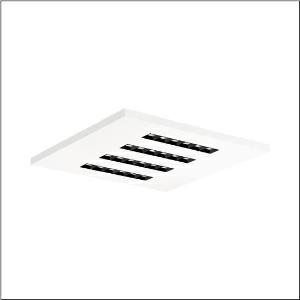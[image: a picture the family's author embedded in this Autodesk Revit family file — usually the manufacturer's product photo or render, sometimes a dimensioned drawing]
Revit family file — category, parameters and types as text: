
# Revit family: silica_r__21_square_51mx6kdu44w_ebd5
name_source: partatom
category: Lighting Fixtures
units: mm (PartAtom-declared; Revit-internal decimal feet)

## family parameters
Cut with Voids When Loaded = No
Host = Face
Light Source = No
Part Type = Normal
Room Calculation Point = No
Round Connector Dimension = Use Diameter
Shared = No

## types (1)
- --- (1 x LED, 4600 lm, 29.6 W, 4000K)
    Apparent Load = 30 VA
    CIE Flux Codes = 86 100 100 100 100
    Color Rendering = 80
    Color Temperature = 4000K
    Default Elevation = 1800 mm
    Description = Silica® 21 Square, office luminaire, primary light control with lens, of PMMA, primary anti-glare with reflector, of PC, black, CAT 2 (L<= 3000cd/m²), light emission: direct distribution, primary light characteristic: symmetric, installation type: lay-in mounting, LED, rated luminous flux: 4.600lm, luminous efficacy: 155lm/W, light colour: 840, colour temperature: 4000K, with terminal, 5-pole, mains connection: 220..240V, AC, 50/60Hz, rated input power: 29.6W, luminaire housing, of sheet steel, coated, traffic white (RAL 9016), module: M625, length: 622mm, width: 622mm, height: 33mm, protection rating (complete): IP20, insulation class (complete): insulation class I (protective earthing), certification: CE, permissible operating ambient temperature: -20..+40°C, standard: EN 50419, packaging unit: 1 piece
    Height = 0 mm  [stored 0 ft]
    Lamp = 1 x LED
    Lamp Light Flux = 4600 lm
    Lamp Power = 29.6 W
    Lamp count = 1
    Length = 622 mm
    Luminous efficacy = 155 lm/W
    Manufacturer = Siteco
    ModVariant = No
    Model = 51MX6KDU44W
    Mounting Place = Ceiling
    Mounting Type = Recessed
    Number of Poles = 1
    OnlyDefault = Yes
    Power Factor = 1
    Product Name = Silica® 21 Square
    Product group = office luminaire | ceiling recessed
    ProductGroupID = 400
    Protection Class = Protection class I
    Protection Degree = IP 20
    RLX_Detail_Level = 1
    RLX_Emergency_Light_Flux = 0 lm
    RLX_Emergency_Type = 0
    RLX_Emergency_Type_DB = No
    RlxData = <blob elided: 41785 chars, md5=ca1c6ae4>
    Socket = socket
    Standby Power = 0 W
    System Light Flux = 4600 lm
    System Power = 30 W
    Type Comments = factory setting: luminous flux: 100 % | dim-lin: 254 | 399 mA
    Type Image = l_1275207.jpg
    URL = http://relux.com
    VarID = @adj_053313
    Voltage = 0 V
    Weight = 0.00 kg
    Width = 622 mm

note: [stored X ft] marks values corroborated as IEEE doubles in the binary element streams (Revit-internal decimal feet)

## geometry (parser evidence)
native form markers: Blend x4, Sweep x9
no freeform markers — native parametric forms only
